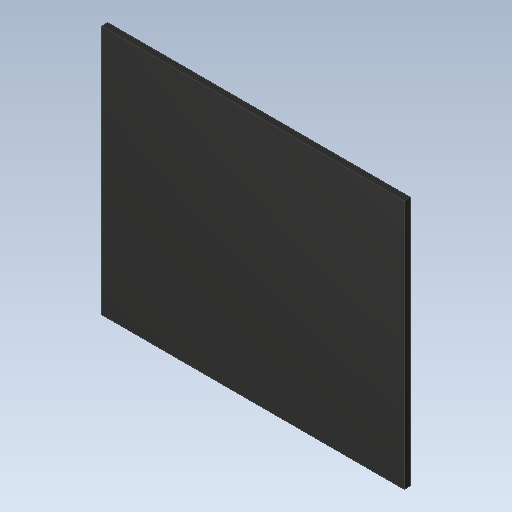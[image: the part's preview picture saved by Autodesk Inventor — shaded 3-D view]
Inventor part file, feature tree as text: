
AUTODESK INVENTOR PART (.ipt)
format: ipt  version: 2020 (Build 240168000, 168)  size: 88,064 bytes
history: imported  units: in
note: dims shown in document units (in); Inventor stores cm internally (conversion verified against a paired STEP export)
features: imported_body x1
ambient origin geometry x8: Origin, YZ Plane, XZ Plane, XY Plane, X Axis, Y Axis, Z Axis, Center Point
bodies: Solid1 (imported_parasolid), Body1 (imported_parasolid)
feature tree (1):
  imported_body  NMx_Import_Brep_tag  [imported B-rep: ~6 faces, bbox_mm=[5.0, 4.1303, 0.1]]
